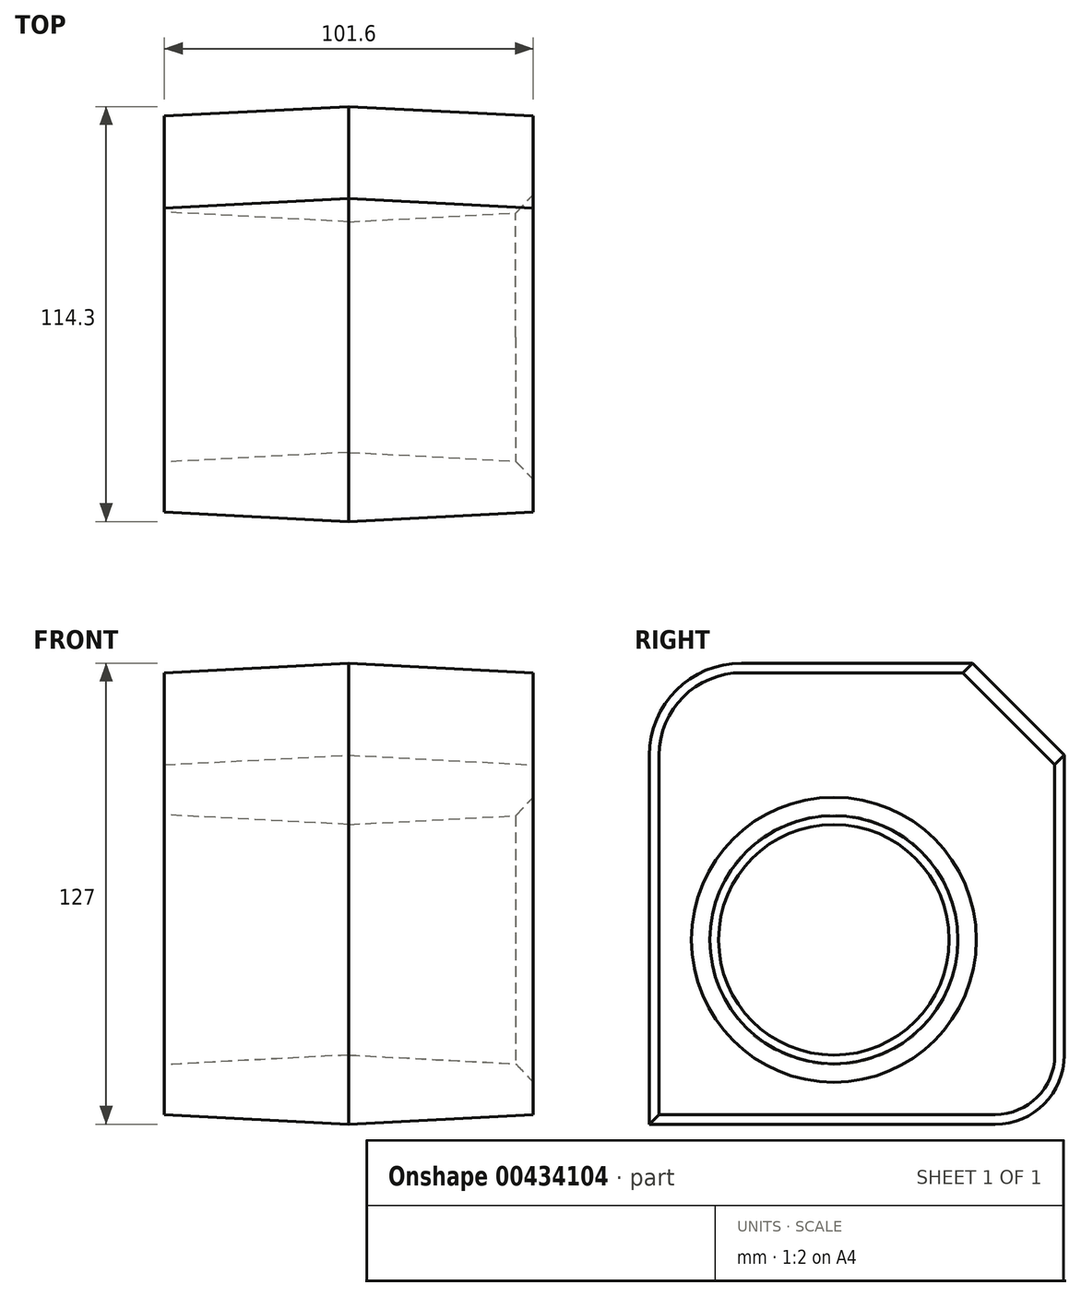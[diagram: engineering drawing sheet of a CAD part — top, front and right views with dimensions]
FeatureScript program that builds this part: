
annotation { "Feature Type Name" : "Feature", "Feature Type Description" : "" }
export const myFeature = defineFeature(function(context is Context, id is Id, definition is map)
    precondition{}
    {
        {
            var Q0;
            Q0=qCreatedBy(makeId("Right.planeOp"),FACE);
            var sketch = newSketch(context, id + "F0", { "sketchPlane" : qUnion([Q0])});
            skLineSegment(sketch, "E0.bottom", {"start": v(-25.4, 76.2) * mm, "end": v(63.5, 76.2) * mm});
            skLineSegment(sketch, "E0.top", {"start": v(-50.8, -50.8) * mm, "end": v(44.45, -50.8) * mm});
            skLineSegment(sketch, "E0.left", {"start": v(-50.8, 50.8) * mm, "end": v(-50.8, -50.8) * mm});
            skLineSegment(sketch, "E0.right", {"start": v(63.5, 76.2) * mm, "end": v(63.5, -31.75) * mm});
            skPoint(sketch, "E1.visualSharp", {"position": v(-50.8, 76.2) * mm});
            skArc(sketch, "E1.filletArc", {"start": v(-25.4, 76.2) * mm, "mid": v(-43.36, 68.76) * mm, "end": v(-50.8, 50.8) * mm});
            skPoint(sketch, "E2.visualSharp", {"position": v(63.5, -50.8) * mm});
            skArc(sketch, "E2.filletArc", {"start": v(44.45, -50.8) * mm, "mid": v(57.92, -45.22) * mm, "end": v(63.5, -31.75) * mm});
            skCircle(sketch, "E3", {"center": v(0, 0) * mm, "radius": 31.75 * mm});
            skSolve(sketch);
        }
        {
            var Q0;
            Q0 = qSketchRegion(id + "F0", true);
            extrude(context, id + "F1", {"entities" : qUnion([Q0]), "endBound" : BoundingType.SYMMETRIC, "depth" : 101.6 * mm, "hasDraft" : true, "draftAngle" : 3 * degree, "draftPullDirection" : true, "hasSecondDirection" : true, "secondDirectionOppositeDirection" : true, "secondDirectionDepth" : 25.4 * mm});
        }
        {
            var Q0;
            Q0=makeQuery(id+"F1.*.split.splitOp","SPLIT",EDGE,{"derivedFrom":makeQuery(id+"F1.opExtrude","SWEPT_EDGE",EDGE,{"disambiguationData":[OSD([sQuery(id+"F0.wireOp",EDGE,"E0.bottom"),sQuery(id+"F0.wireOp",EDGE,"E0.right")])]})});
            var Q1;
            Q1=makeQuery(id+"F1.*.split.splitOp","SPLIT",EDGE,{"derivedFrom":makeQuery(id+"F1.opExtrude","SWEPT_EDGE",EDGE,{"disambiguationData":[OSD([sQuery(id+"F0.wireOp",EDGE,"E0.bottom"),sQuery(id+"F0.wireOp",EDGE,"E0.right")])]}),"isFromBackBody":true});
            chamfer(context, id + "F2", {"entities" : qUnion([Q0, Q1]), "width" : 25.4 * mm, "tangentPropagation" : true});
        }
        {
            var Q0;
            Q0=makeQuery(id+"F1.opExtrude","CAP_EDGE",EDGE,{"disambiguationData":[OSD([sQuery(id+"F0.wireOp",EDGE,"E3")])],"isStart":false});
            chamfer(context, id + "F3", {"entities" : qUnion([Q0]), "width" : 5.08 * mm, "tangentPropagation" : true});
        }
    });
